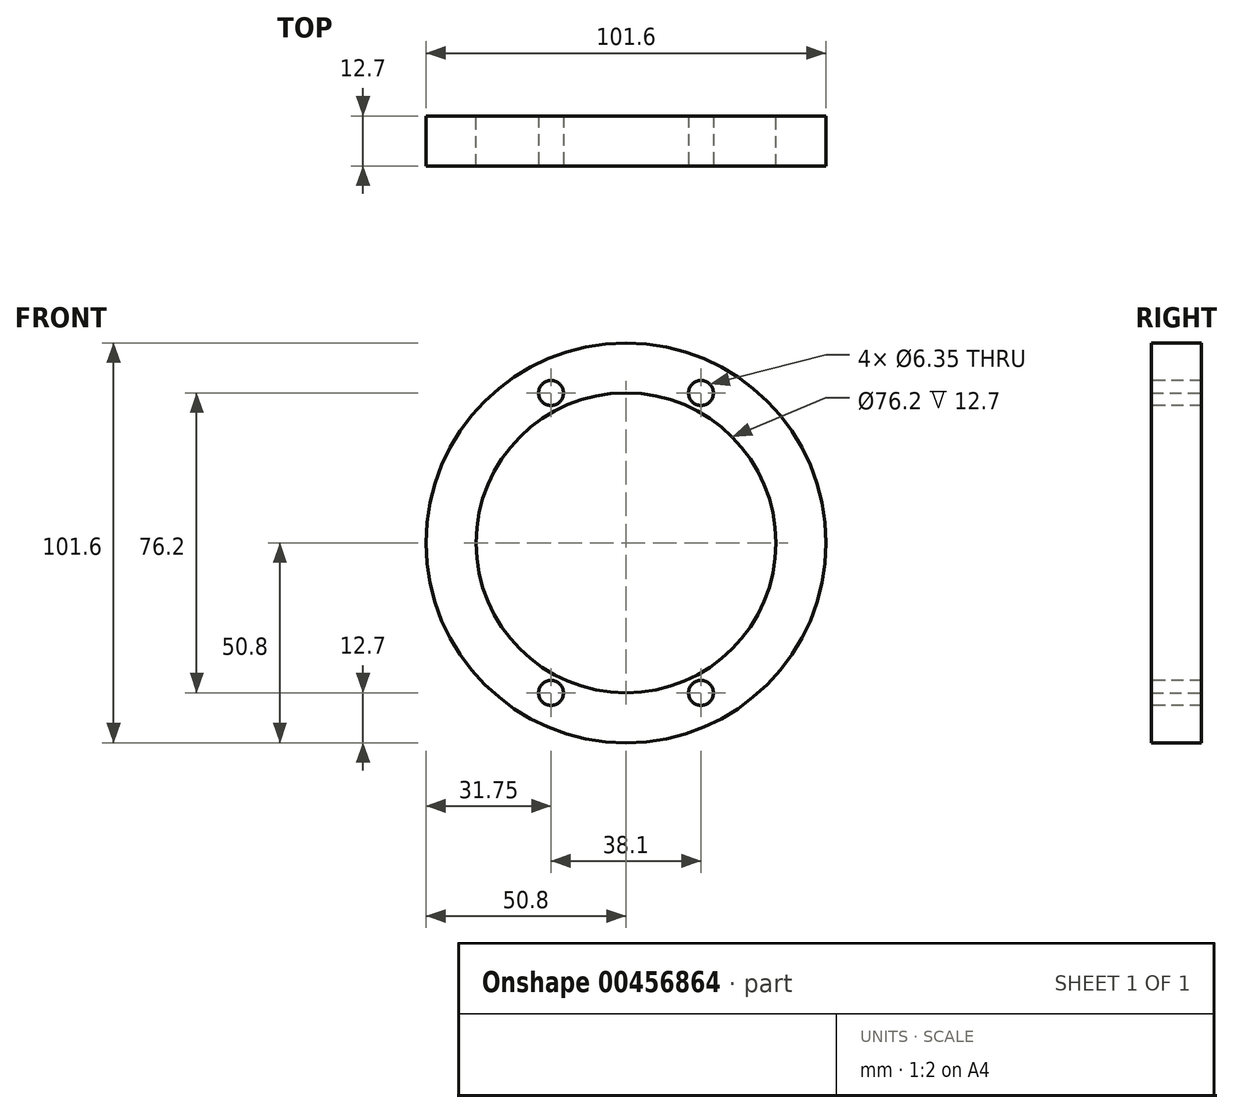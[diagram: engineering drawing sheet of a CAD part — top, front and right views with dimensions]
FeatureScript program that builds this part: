
annotation { "Feature Type Name" : "Feature", "Feature Type Description" : "" }
export const myFeature = defineFeature(function(context is Context, id is Id, definition is map)
    precondition{}
    {
        {
            var Q0;
            Q0=qCreatedBy(makeId("Front.planeOp"),FACE);
            var sketch = newSketch(context, id + "F0", { "sketchPlane" : qUnion([Q0])});
            skCircle(sketch, "E0", {"center": v(0, 0) * mm, "radius": 50.8 * mm});
            skCircle(sketch, "E1", {"center": v(0, 0) * mm, "radius": 38.1 * mm});
            skCircle(sketch, "E2", {"center": v(0, 0) * mm, "radius": 34.93 * mm, "construction": true});
            skPoint(sketch, "E3", {"position": v(0, 34.93) * mm});
            skPoint(sketch, "E4", {"position": v(-34.93, 0) * mm});
            skPoint(sketch, "E5", {"position": v(0, -34.92) * mm});
            skPoint(sketch, "E6", {"position": v(34.93, 0) * mm});
            skSolve(sketch);
        }
        {
            var Q0;
            Q0=qSketchRegion(id+"F0",true);
            extrude(context, id + "F1", {"entities" : qUnion([Q0]), "depth" : 12.7 * mm});
        }
        {
            var Q0;
            Q0=makeQuery(id+"F1.opExtrude","CAP_FACE",FACE,{"disambiguationData":[OSD([sQuery(id+"F0.wireOp",EDGE,"E0"),sQuery(id+"F0.wireOp",EDGE,"E1")])],"isStart":false});
            var sketch = newSketch(context, id + "F2", { "sketchPlane" : qUnion([Q0])});
            skCircle(sketch, "E7", {"center": v(-19.05, 38.1) * mm, "radius": 3.18 * mm});
            skCircle(sketch, "E8", {"center": v(19.05, 38.1) * mm, "radius": 3.18 * mm});
            skCircle(sketch, "E9", {"center": v(19.05, -38.1) * mm, "radius": 3.18 * mm});
            skCircle(sketch, "E10", {"center": v(-19.05, -38.1) * mm, "radius": 3.18 * mm});
            skLineSegment(sketch, "E11.bottom", {"start": v(-19.05, -38.1) * mm, "end": v(19.05, -38.1) * mm, "construction": true});
            skLineSegment(sketch, "E11.top", {"start": v(-19.05, 38.1) * mm, "end": v(19.05, 38.1) * mm, "construction": true});
            skLineSegment(sketch, "E11.left", {"start": v(-19.05, -38.1) * mm, "end": v(-19.05, 38.1) * mm, "construction": true});
            skLineSegment(sketch, "E11.right", {"start": v(19.05, -38.1) * mm, "end": v(19.05, 38.1) * mm, "construction": true});
            skSolve(sketch);
        }
        {
            var Q0;
            Q0=qSketchRegion(id+"F2",true);
            extrude(context, id + "F3", {"entities" : qUnion([Q0]), "operationType" : NewBodyOperationType.REMOVE, "oppositeDirection" : true, "depth" : 12.7 * mm});
        }
    });
